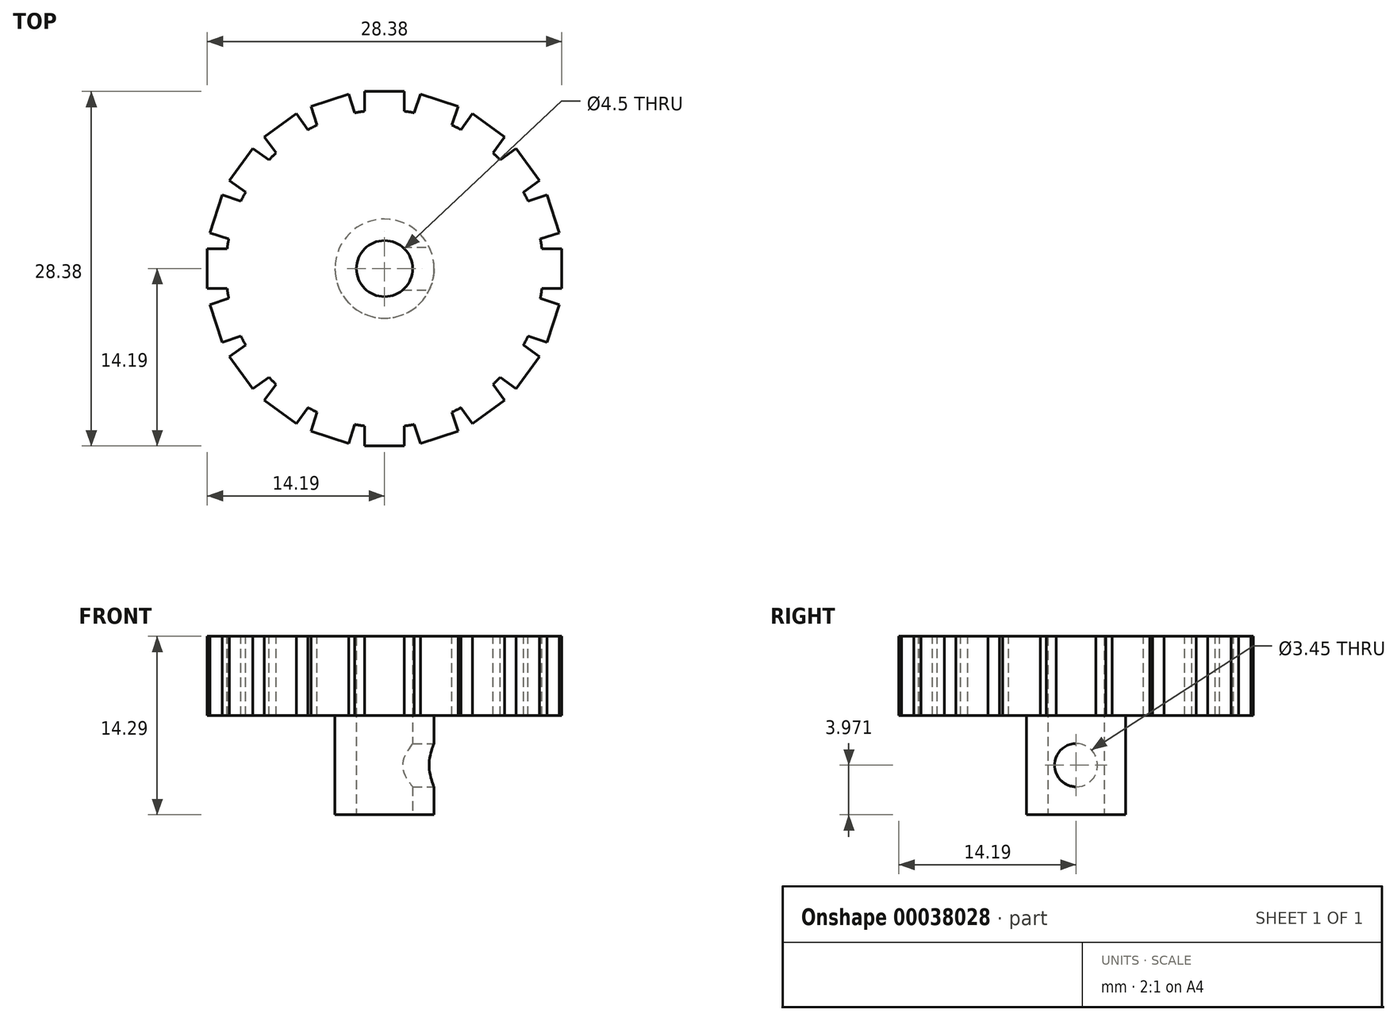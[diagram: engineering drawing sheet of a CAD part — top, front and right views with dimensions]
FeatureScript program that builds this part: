
annotation { "Feature Type Name" : "Feature", "Feature Type Description" : "" }
export const myFeature = defineFeature(function(context is Context, id is Id, definition is map)
    precondition{}
    {
        {
            var Q0;
            Q0=qCreatedBy(makeId("Top.planeOp"),FACE);
            var sketch = newSketch(context, id + "F0", { "sketchPlane" : qUnion([Q0])});
            skCircle(sketch, "E0", {"center": v(0, 0) * mm, "radius": 12.7 * mm});
            skCircle(sketch, "E1", {"center": v(0, 0) * mm, "radius": 2.25 * mm});
            skSolve(sketch);
        }
        {
            var Q0;
            Q0=qSketchRegion(id+"F0",true);
            extrude(context, id + "F1", {"entities" : qUnion([Q0]), "depth" : 6.35 * mm});
        }
        {
            var Q0;
            Q0=makeQuery(id+"F1.opExtrude","CAP_FACE",FACE,{"disambiguationData":[OSD([sQuery(id+"F0.wireOp",EDGE,"E0"),sQuery(id+"F0.wireOp",EDGE,"E1")])],"isStart":true});
            var sketch = newSketch(context, id + "F2", { "sketchPlane" : qUnion([Q0])});
            skCircle(sketch, "E2", {"center": v(0, 0) * mm, "radius": 2.25 * mm});
            skLineSegment(sketch, "E3.rect.bottom", {"start": v(3.97, 3.97) * mm, "end": v(-3.97, 3.97) * mm});
            skLineSegment(sketch, "E3.rect.top", {"start": v(3.97, -3.97) * mm, "end": v(-3.97, -3.97) * mm});
            skLineSegment(sketch, "E3.rect.left", {"start": v(3.97, 3.97) * mm, "end": v(3.97, -3.97) * mm});
            skLineSegment(sketch, "E3.rect.right", {"start": v(-3.97, 3.97) * mm, "end": v(-3.97, -3.97) * mm});
            skSolve(sketch);
        }
        {
            var Q0;
            Q0=qSketchRegion(id+"F2",true);
            extrude(context, id + "F3", {"entities" : qUnion([Q0]), "operationType" : NewBodyOperationType.ADD, "depth" : 7.94 * mm});
        }
        {
            var Q0;
            Q0=makeQuery(id+"F3.opExtrude","SWEPT_FACE",FACE,{"disambiguationData":[OSD([sQuery(id+"F2.wireOp",EDGE,"E3.rect.left")])]});
            var sketch = newSketch(context, id + "F4", { "sketchPlane" : qUnion([Q0])});
            skLineSegment(sketch, "E4", {"start": v(3.97, -3.97) * mm, "end": v(-3.97, -3.97) * mm});
            skCircle(sketch, "E5", {"center": v(0, -3.97) * mm, "radius": 1.73 * mm});
            skSolve(sketch);
        }
        {
            var Q0;
            Q0=qSketchRegion(id+"F4",true);
            var Q1;
            Q1=makeQuery(id+"F3.boolean.opBoolean","MERGE",FACE,{"derivedFrom":[makeQuery(id+"F1.opExtrude","SWEPT_FACE",FACE,{"disambiguationData":[OSD([sQuery(id+"F0.wireOp",EDGE,"E1")])]}),makeQuery(id+"F3.opExtrude","SWEPT_FACE",FACE,{"disambiguationData":[OSD([sQuery(id+"F2.wireOp",EDGE,"E2")])]})]});
            extrude(context, id + "F5", {"entities" : qUnion([Q0]), "operationType" : NewBodyOperationType.REMOVE, "endBound" : BoundingType.UP_TO_SURFACE, "oppositeDirection" : true, "endBoundEntityFace" : qUnion([Q1]), "depth" : 25.4 * mm});
        }
        {
            var Q0;
            Q0=makeQuery(id+"F3.opExtrude","SWEPT_EDGE",EDGE,{"disambiguationData":[OSD([sQuery(id+"F2.wireOp",EDGE,"E3.rect.top"),sQuery(id+"F2.wireOp",EDGE,"E3.rect.left")])]});
            var Q1;
            Q1=makeQuery(id+"F3.opExtrude","SWEPT_EDGE",EDGE,{"disambiguationData":[OSD([sQuery(id+"F2.wireOp",EDGE,"E3.rect.top"),sQuery(id+"F2.wireOp",EDGE,"E3.rect.right")])]});
            var Q2;
            Q2=makeQuery(id+"F3.opExtrude","SWEPT_EDGE",EDGE,{"disambiguationData":[OSD([sQuery(id+"F2.wireOp",EDGE,"E3.rect.bottom"),sQuery(id+"F2.wireOp",EDGE,"E3.rect.right")])]});
            var Q3;
            Q3=makeQuery(id+"F3.opExtrude","SWEPT_EDGE",EDGE,{"disambiguationData":[OSD([sQuery(id+"F2.wireOp",EDGE,"E3.rect.bottom"),sQuery(id+"F2.wireOp",EDGE,"E3.rect.left")])]});
            fillet(context, id + "F6", {"entities" : qUnion([Q0, Q1, Q2, Q3]), "radius" : 3.97 * mm, "tangentPropagation" : true, "allowEdgeOverflow" : false});
        }
        {
            var Q0;
            Q0=makeQuery(id+"F1.opExtrude","CAP_FACE",FACE,{"disambiguationData":[OSD([sQuery(id+"F0.wireOp",EDGE,"E0"),sQuery(id+"F0.wireOp",EDGE,"E1")])],"isStart":false});
            var sketch = newSketch(context, id + "F7", { "sketchPlane" : qUnion([Q0])});
            skLineSegment(sketch, "E6.bottom", {"start": v(12.6, 1.59) * mm, "end": v(14.19, 1.59) * mm});
            skLineSegment(sketch, "E6.top", {"start": v(12.6, -1.59) * mm, "end": v(14.19, -1.59) * mm});
            skLineSegment(sketch, "E6.left", {"start": v(12.6, 1.59) * mm, "end": v(12.6, -1.59) * mm});
            skLineSegment(sketch, "E6.right", {"start": v(14.19, 1.59) * mm, "end": v(14.19, -1.59) * mm});
            skLineSegment(sketch, "E7", {"start": v(12.6, 0) * mm, "end": v(0, 0) * mm, "construction": true});
            skPoint(sketch, "E7.endSnap0", {"position": v(12.6, 0) * mm});
            skSolve(sketch);
        }
        {
            var Q0;
            Q0=qSketchRegion(id+"F7",true);
            var Q1;
            Q1=makeQuery(id+"F1.opExtrude","CAP_FACE",FACE,{"disambiguationData":[OSD([sQuery(id+"F0.wireOp",EDGE,"E0"),sQuery(id+"F0.wireOp",EDGE,"E1")])],"isStart":true});
            extrude(context, id + "F8", {"entities" : qUnion([Q0]), "operationType" : NewBodyOperationType.ADD, "endBound" : BoundingType.UP_TO_SURFACE, "oppositeDirection" : true, "endBoundEntityFace" : qUnion([Q1]), "depth" : 25.4 * mm});
        }
        {
            var Q0;
            Q0=makeQuery(id+"F8.opExtrude","SWEPT_FACE",FACE,{"disambiguationData":[OSD([sQuery(id+"F7.wireOp",EDGE,"E6.right")])]});
            var Q1;
            Q1=makeQuery(id+"F8.opExtrude","SWEPT_FACE",FACE,{"disambiguationData":[OSD([sQuery(id+"F7.wireOp",EDGE,"E6.top")])]});
            var Q2;
            Q2=makeQuery(id+"F8.opExtrude","SWEPT_FACE",FACE,{"disambiguationData":[OSD([sQuery(id+"F7.wireOp",EDGE,"E6.bottom")])]});
            var Q3;
            Q3=makeQuery(id+"F1.opExtrude","SWEPT_FACE",FACE,{"disambiguationData":[OSD([sQuery(id+"F0.wireOp",EDGE,"E0")])]});
            circularPattern(context, id + "F9", {"faces" : qUnion([Q0, Q1, Q2]), "axis" : qUnion([Q3]), "angle" : 18 * degree, "instanceCount" : round(20), "patternType" : PatternType.FACE});
        }
    });
